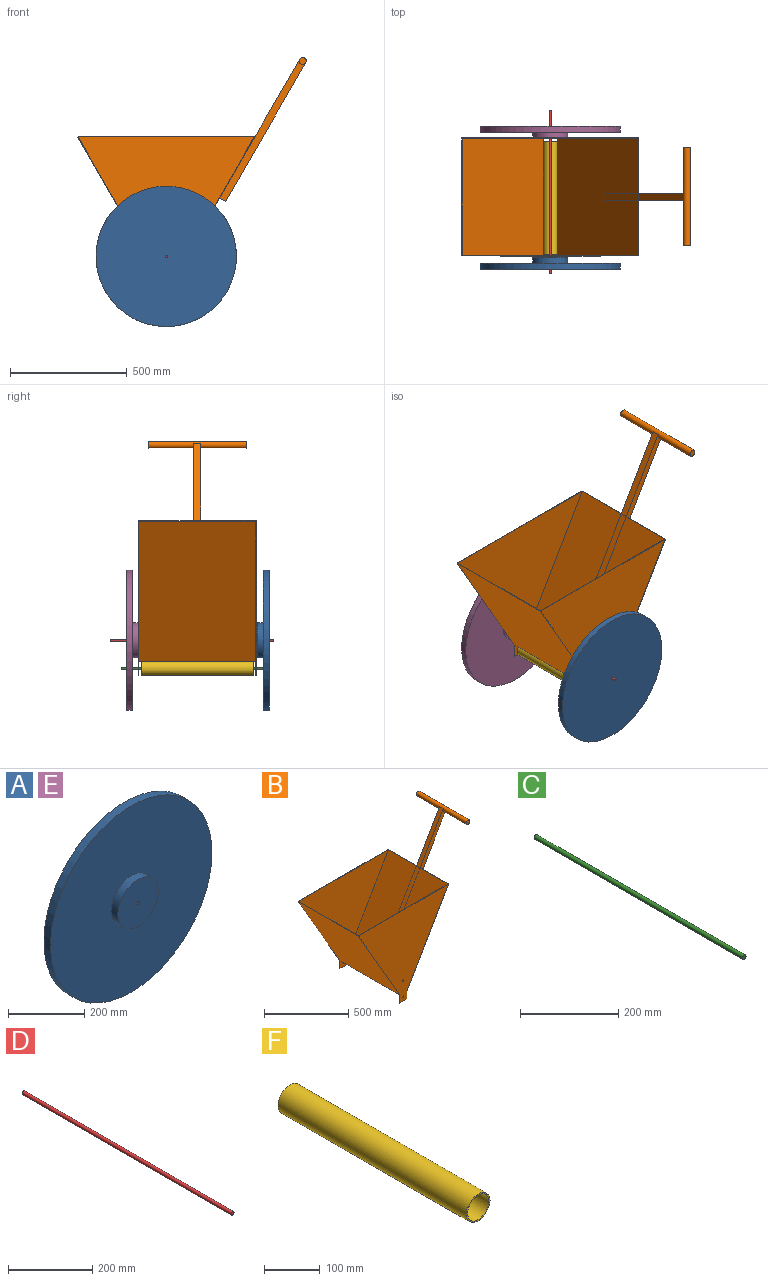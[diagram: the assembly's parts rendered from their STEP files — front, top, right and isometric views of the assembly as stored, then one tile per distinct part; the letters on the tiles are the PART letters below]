
ASSEMBLY  parts=6 mates=5
PART A: 6 faces, bbox 600x50x600 mm
  f0: cylinder r=300mm len=600mm, axis (0,-1,0), area 47123.9mm2, adj f2,f3
  f1: cylinder r=5mm len=50mm, axis (0,-1,0), area 1570.8mm2, adj f2,f5
  f2: plane 600x600mm, normal (0,1,0), area 282664.8mm2, adj f0,f1
  f3: plane 600x600mm, normal (0,-1,0), area 265071.9mm2, adj f0,f4
  f4: cylinder r=75mm len=150mm, axis (0,1,0), area 11781mm2, adj f3,f5
  f5: plane 150x150mm, normal (0,-1,0), area 17592.9mm2, adj f1,f4
PART B: 32 faces, bbox 976.8x504x1000.5 mm
  f0: plane 752.82x660.54mm, normal (0,-1,0), area 247321.2mm2, adj f1,f2,f3,f7,f12,f13,f21,f23
  f1: plane 60.54x2mm, normal (-1,0,0), area 121.1mm2, adj f0,f2,f10,f11
  f2: plane 60x2mm, normal (0,0,-1), area 120mm2, adj f0,f1,f3,f11
  f3: plane 60.54x2mm, normal (1,0,0), area 121.1mm2, adj f0,f2,f4,f11
  f4: plane 504x2mm, normal (-0.26,0,-0.97), area 1043.6mm2, adj f3,f5,f11,f13,f17,f19
  f5: plane 599.54x504mm, normal (0.87,0,-0.5), area 339911.3mm2, adj f4,f6,f11,f19,f25,f28,f29
  f6: plane 504x1.73mm, normal (0.5,0,0.87), area 1008mm2, adj f5,f7,f11,f13,f18,f19,f24
  f7: plane 752.82x2mm, normal (0,0,1), area 1505.6mm2, adj f0,f6,f8,f11
  f8: plane 504x1.73mm, normal (-0.5,0,0.87), area 1008mm2, adj f7,f9,f11,f12,f18,f19
  f9: plane 599.54x504mm, normal (-0.87,0,-0.5), area 348911.3mm2, adj f8,f10,f11,f19
  f10: plane 504x2mm, normal (0.26,0,-0.97), area 1043.6mm2, adj f1,f9,f11,f12,f15,f19
  f11: plane 756.28x660.54mm, normal (0,1,0), area 250091.4mm2, adj f1,f2,f3,f4,f5,f6,f7,f8
  f12: plane 600x500mm, normal (0.87,0,0.5), area 346410.2mm2, adj f0,f8,f10,f14
  f13: plane 600x500mm, normal (-0.87,0,0.5), area 346410.2mm2, adj f0,f4,f6,f14
  f14: plane 752.82x660.54mm, normal (0,1,0), area 247321.2mm2, adj f12,f13,f15,f16,f17,f18,f20,f22
  f15: plane 60.54x2mm, normal (-1,0,0), area 121.1mm2, adj f10,f14,f16,f19
  f16: plane 60x2mm, normal (0,0,-1), area 120mm2, adj f14,f15,f17,f19
  f17: plane 60.54x2mm, normal (1,0,0), area 121.1mm2, adj f4,f14,f16,f19
  f18: plane 752.82x2mm, normal (0,0,1), area 1505.6mm2, adj f6,f8,f14,f19
  f19: plane 756.28x660.54mm, normal (0,-1,0), area 250091.4mm2, adj f4,f5,f6,f8,f9,f10,f15,f16
  f20: cylinder r=5mm len=10mm, axis (0,-1,0), area 62.8mm2, adj f14,f19
  f21: cylinder r=5mm len=10mm, axis (0,-1,0), area 62.8mm2, adj f0,f11
  f22: cylinder r=5mm len=10mm, axis (0,1,0), area 62.8mm2, adj f14,f19
  f23: cylinder r=5mm len=10mm, axis (0,1,0), area 62.8mm2, adj f0,f11
  f24: plane 333.42x192.5mm, normal (-0.87,0,0.5), area 11550mm2, adj f6,f25,f28,f31
  f25: plane 608.23x368.48mm, normal (0,1,0), area 20196.6mm2, adj f5,f24,f29,f30,f31
  f26: plane 30x30mm, normal (0,1,0), area 706.9mm2, adj f31
  f27: plane 30x30mm, normal (0,-1,0), area 706.9mm2, adj f31
  f28: plane 608.23x368.48mm, normal (0,-1,0), area 20196.6mm2, adj f5,f24,f29,f30,f31
  f29: plane 30x25.98mm, normal (-0.5,0,-0.87), area 900mm2, adj f5,f25,f28,f30
  f30: plane 593.23x342.5mm, normal (0.87,0,-0.5), area 20550mm2, adj f25,f28,f29,f31
  f31: cylinder r=15mm len=420mm, axis (0,-1,0), area 38170.4mm2, adj f24,f25,f26,f27,f28,f30
PART C: 3 faces, bbox 10x600x10 mm
  f0: cylinder r=5mm len=600mm, axis (0,1,0), area 18849.6mm2, adj f1,f2
  f1: plane 10x10mm, normal (0,-1,0), area 78.5mm2, adj f0
  f2: plane 10x10mm, normal (0,1,0), area 78.5mm2, adj f0
PART D: 3 faces, bbox 10x700x10 mm
  f0: cylinder r=5mm len=700mm, axis (0,1,0), area 21991.1mm2, adj f1,f2
  f1: plane 10x10mm, normal (0,-1,0), area 78.5mm2, adj f0
  f2: plane 10x10mm, normal (0,1,0), area 78.5mm2, adj f0
PART E: same geometry as A
PART F: 4 faces, bbox 60x480x60 mm
  f0: cylinder r=27mm len=480mm, axis (0,1,0), area 81430.1mm2, adj f2,f3
  f1: cylinder r=30mm len=480mm, axis (0,1,0), area 90477.9mm2, adj f2,f3
  f2: plane 60x60mm, normal (0,-1,0), area 537.2mm2, adj f0,f1
  f3: plane 60x60mm, normal (0,1,0), area 537.2mm2, adj f0,f1
PLACE A rot(axis=(1,0,-0.05),180deg) t=(394.55,-533,66.64)mm
PLACE B t=(-13.85,0,-80.93)mm fixed
PLACE C rot(axis=(0,-1,0),170deg) t=(-8.64,20,-21.38)mm
PLACE D rot(axis=(0,1,0),5.5deg) t=(-28.29,20,-80.23)mm
PLACE E rot(axis=(0,-1,0),105deg) t=(-83.46,27,471.5)mm
PLACE F t=(-13.85,-3,-80.93)mm
MATE cylindrical E.f0 <-> D.f0  axis (0,1,0) through (-13.85,52,69.07)mm
MATE revolute F.f0 <-> C.f0  axis (0,1,0) through (-13.85,-13,-50.93)mm
MATE revolute D.f0 <-> B.f22  axis (0,1,0) through (-13.85,-228,69.07)mm
MATE cylindrical A.f0 <-> D.f0  axis (0,-1,0) through (-13.85,-558,69.07)mm
MATE revolute C.f0 <-> B.f20  axis (0,1,0) through (-13.85,-228,-50.93)mm
